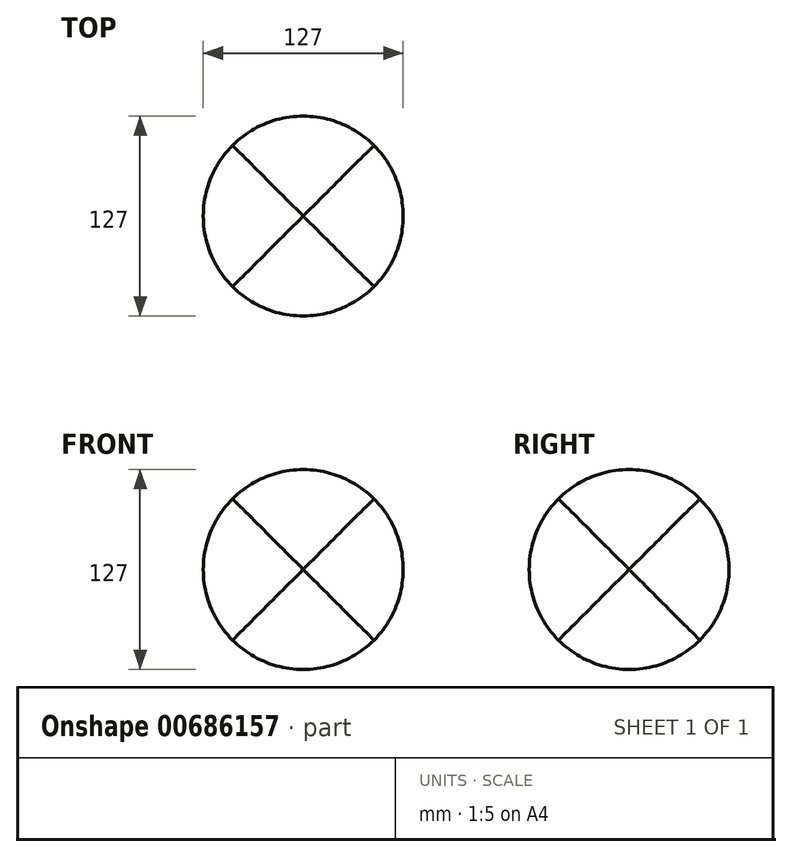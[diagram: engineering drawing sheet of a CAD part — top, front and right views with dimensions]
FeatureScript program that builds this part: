
annotation { "Feature Type Name" : "Feature", "Feature Type Description" : "" }
export const myFeature = defineFeature(function(context is Context, id is Id, definition is map)
    precondition{}
    {
        {
            var Q0;
            Q0=qCreatedBy(makeId("Front.planeOp"),FACE);
            var sketch = newSketch(context, id + "F0", { "sketchPlane" : qUnion([Q0])});
            skCircle(sketch, "E0", {"center": v(0, 0) * mm, "radius": 63.5 * mm});
            skSolve(sketch);
        }
        {
            var Q0;
            Q0=makeQuery(id+"F0.imprint","IMPRINT",FACE,{"disambiguationData":[TD([[makeQuery(id+"F0.imprint","IMPRINT",EDGE,{"derivedFrom":sQuery(id+"F0.wireOp",EDGE,"E0")}),1.0]])]});
            extrude(context, id + "F1", {"entities" : qUnion([Q0]), "depth" : 127 * mm, "offsetDistance" : 25.4 * mm, "symmetric" : true});
        }
        {
            var Q0;
            Q0=qCreatedBy(makeId("Top.planeOp"),FACE);
            var sketch = newSketch(context, id + "F2", { "sketchPlane" : qUnion([Q0])});
            skCircle(sketch, "E1", {"center": v(0, 0) * mm, "radius": 63.5 * mm});
            skLineSegment(sketch, "E2.bottom", {"start": v(104.96, 94.32) * mm, "end": v(-104.96, 94.32) * mm});
            skLineSegment(sketch, "E2.top", {"start": v(104.96, -94.32) * mm, "end": v(-104.96, -94.32) * mm});
            skLineSegment(sketch, "E2.left", {"start": v(104.96, 94.32) * mm, "end": v(104.96, -94.32) * mm});
            skLineSegment(sketch, "E2.right", {"start": v(-104.96, 94.32) * mm, "end": v(-104.96, -94.32) * mm});
            skSolve(sketch);
        }
        {
            var Q0;
            Q0=makeQuery(id+"F2.imprint","IMPRINT",FACE,{"disambiguationData":[TD([[makeQuery(id+"F2.imprint","IMPRINT",EDGE,{"derivedFrom":sQuery(id+"F2.wireOp",EDGE,"E1")}),-1.0]])]});
            extrude(context, id + "F3", {"entities" : qUnion([Q0]), "operationType" : NewBodyOperationType.REMOVE, "oppositeDirection" : true, "depth" : 127 * mm, "offsetDistance" : 25.4 * mm, "symmetric" : true});
        }
        {
            var Q0;
            Q0=qCreatedBy(makeId("Right.planeOp"),FACE);
            var sketch = newSketch(context, id + "F4", { "sketchPlane" : qUnion([Q0])});
            skCircle(sketch, "E3", {"center": v(0, 0) * mm, "radius": 63.5 * mm});
            skLineSegment(sketch, "E4.bottom", {"start": v(-77.48, 76.28) * mm, "end": v(77.48, 76.28) * mm});
            skLineSegment(sketch, "E4.top", {"start": v(-77.48, -76.28) * mm, "end": v(77.48, -76.28) * mm});
            skLineSegment(sketch, "E4.left", {"start": v(-77.48, 76.28) * mm, "end": v(-77.48, -76.28) * mm});
            skLineSegment(sketch, "E4.right", {"start": v(77.48, 76.28) * mm, "end": v(77.48, -76.28) * mm});
            skSolve(sketch);
        }
        {
            var Q0;
            Q0 = qSketchRegion(id + "F4", true);
            extrude(context, id + "F5", {"entities" : qUnion([Q0]), "operationType" : NewBodyOperationType.REMOVE, "oppositeDirection" : true, "depth" : 127 * mm, "offsetDistance" : 25.4 * mm, "symmetric" : true});
        }
    });
